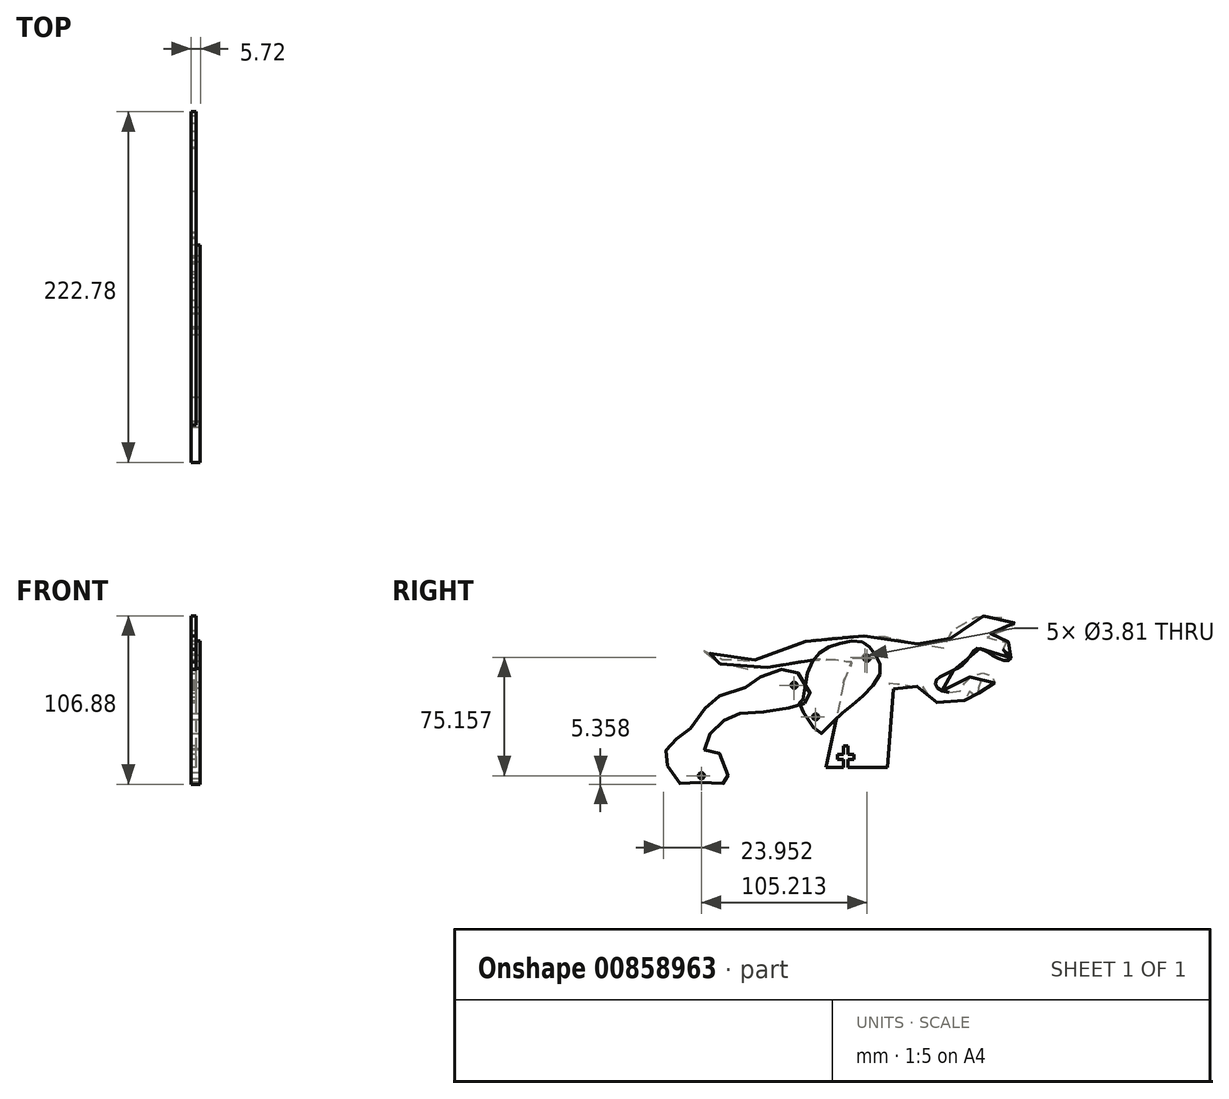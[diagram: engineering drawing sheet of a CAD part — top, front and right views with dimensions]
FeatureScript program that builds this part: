
annotation { "Feature Type Name" : "Feature", "Feature Type Description" : "" }
export const myFeature = defineFeature(function(context is Context, id is Id, definition is map)
    precondition{}
    {
        {
            var Q0;
            Q0=qCreatedBy(makeId("Right.planeOp"),FACE);
            var sketch = newSketch(context, id + "F0", { "sketchPlane" : qUnion([Q0])});
            skLineSegment(sketch, "E0.bottom", {"start": v(-101.6, -58.23) * mm, "end": v(101.6, -58.23) * mm});
            skLineSegment(sketch, "E0.top", {"start": v(-101.6, 43.37) * mm, "end": v(101.6, 43.37) * mm});
            skLineSegment(sketch, "E0.left", {"start": v(-101.6, -58.23) * mm, "end": v(-101.6, 43.37) * mm});
            skLineSegment(sketch, "E0.right", {"start": v(101.6, -58.23) * mm, "end": v(101.6, 43.37) * mm});
            skFitSpline(sketch, "E1", {"points": [v(-99.09, 21.53) * mm, v(-88.71, 16.38) * mm, v(-70.91, 13.77) * mm, v(-51.8, 19.14) * mm, v(-25.55, 28.4) * mm, v(4.08, 29.94) * mm, v(29.4, 27.78) * mm, v(49.76, 21.92) * mm, v(57.79, 25) * mm, v(61.18, 35.19) * mm, v(76.93, 42.29) * mm, v(90.82, 41.98) * mm, v(98.84, 39.51) * mm, v(99.63, 37.46) * mm, v(98.96, 34.1) * mm, v(95.6, 33.6) * mm, v(81.8, 30.57) * mm, v(82.64, 28.88) * mm, v(90.38, 25.01) * mm, v(97.27, 26.7) * mm, v(92.4, 21.82) * mm, v(96.94, 17.28) * mm, v(96.1, 14.42) * mm, v(86, 17.44) * mm, v(75.74, 22.15) * mm, v(70.19, 15.26) * mm, v(58.41, 7.01) * mm, v(49.67, 1.46) * mm, v(51.85, -3.92) * mm, v(64.97, -5.1) * mm, v(68.84, 1.63) * mm, v(79.27, 6.34) * mm, v(86.5, 3.31) * mm, v(86.84, 0) * mm, v(83.14, 1.63) * mm, v(76.92, 0) * mm, v(76.92, -6.78) * mm, v(73.9, -8.46) * mm, v(72.04, -4.43) * mm, v(67.33, -11.66) * mm, v(64.97, -11.66) * mm, v(54.71, -11.32) * mm, v(49.16, -12) * mm, v(42.1, -2.74) * mm, v(41.6, -1.4) * mm, v(33.68, -2.24) * mm, v(20.06, 0) * mm, v(22.74, -3.75) * mm, v(0, -3.58) * mm, v(-8.88, 0) * mm, v(-3.5, 12.9) * mm, v(-5.68, 13.4) * mm, v(-10.9, 14.25) * mm, v(-31.08, 14.75) * mm, v(-49.08, 11.9) * mm, v(-66.3, 8.68) * mm, v(-86.1, 11.83) * mm, v(-99.09, 20.33) * mm, v(-99.09, 21.53) * mm]});
            skLineSegment(sketch, "E2", {"start": v(-8.88, 0) * mm, "end": v(-8.88, -0.42) * mm});
            skLineSegment(sketch, "E3", {"start": v(-6.19, -53.65) * mm, "end": v(19.06, -53.65) * mm});
            skLineSegment(sketch, "E4", {"start": v(19.06, -53.65) * mm, "end": v(22.74, -3.75) * mm});
            skPoint(sketch, "E5", {"position": v(5.1, -53.65) * mm});
            skPoint(sketch, "E6", {"position": v(11.44, -53.65) * mm});
            skPoint(sketch, "E7", {"position": v(-1.26, -53.65) * mm});
            skLineSegment(sketch, "E8.bottom", {"start": v(-1.26, -53.65) * mm, "end": v(11.44, -53.65) * mm});
            skLineSegment(sketch, "E8.top", {"start": v(-1.26, -57.46) * mm, "end": v(11.44, -57.46) * mm});
            skLineSegment(sketch, "E8.left", {"start": v(-1.26, -53.65) * mm, "end": v(-1.26, -57.46) * mm});
            skLineSegment(sketch, "E8.right", {"start": v(11.44, -53.65) * mm, "end": v(11.44, -57.46) * mm});
            skFitSpline(sketch, "E9", {"points": [v(-38.83, -1.02) * mm, v(-43.34, -9.03) * mm, v(-45.18, -18.35) * mm, v(-45.97, -18.87) * mm, v(-38.83, -29.37) * mm, v(-37.3, -28.72) * mm, v(-32.31, -23.6) * mm, v(-23.65, -16.25) * mm, v(-17.22, -7.19) * mm, v(-19.58, -1.02) * mm, v(-23.39, 2.79) * mm, v(-31.26, 2.4) * mm, v(-38.83, -1.02) * mm]});
            skFitSpline(sketch, "E10", {"points": [v(-69.17, -12.02) * mm, v(-65.16, -9.2) * mm, v(-59.21, -6.38) * mm, v(-52.14, -5.65) * mm, v(-49.52, -9.26) * mm, v(-45.79, -16) * mm, v(-48.07, -17.65) * mm, v(-51.2, -18.53) * mm, v(-57.32, -20.03) * mm, v(-68.85, -21.17) * mm, v(-73.17, -21.7) * mm, v(-77.93, -24.73) * mm, v(-82.13, -29.08) * mm, v(-83.8, -34) * mm, v(-82.63, -33.83) * mm, v(-78.1, -35.68) * mm, v(-75.34, -43.63) * mm, v(-75.27, -45.77) * mm, v(-78.96, -45.77) * mm, v(-87.61, -45.77) * mm, v(-92.9, -45.77) * mm, v(-97.04, -39.01) * mm, v(-97.84, -34.82) * mm, v(-95.26, -33.16) * mm, v(-92.9, -29.4) * mm, v(-89.03, -26.91) * mm, v(-83.5, -19.37) * mm, v(-79.67, -15.56) * mm, v(-69.17, -12.02) * mm]});
            skCircle(sketch, "E11", {"center": v(-84.74, -43.25) * mm, "radius": 1.06 * mm});
            skCircle(sketch, "E12", {"center": v(-52.03, -11.32) * mm, "radius": 1.06 * mm});
            skCircle(sketch, "E13", {"center": v(-40.2, -23.6) * mm, "radius": 1.06 * mm});
            skCircle(sketch, "E14", {"center": v(-22.06, -2.93) * mm, "radius": 1.06 * mm});
            skLineSegment(sketch, "E15", {"start": v(-20.2, -53.65) * mm, "end": v(-9.03, -53.65) * mm});
            skLineSegment(sketch, "E16", {"start": v(-8.88, -0.42) * mm, "end": v(-20.2, -53.65) * mm});
            skPoint(sketch, "E17", {"position": v(-6.19, -53.65) * mm});
            skLineSegment(sketch, "E18", {"start": v(-6.19, -53.65) * mm, "end": v(-6.19, -48.57) * mm});
            skLineSegment(sketch, "E19", {"start": v(-6.19, -48.57) * mm, "end": v(-2.28, -48.57) * mm});
            skLineSegment(sketch, "E20", {"start": v(-2.28, -48.57) * mm, "end": v(-2.28, -45.4) * mm});
            skLineSegment(sketch, "E21", {"start": v(-2.28, -45.4) * mm, "end": v(-6.19, -45.4) * mm});
            skLineSegment(sketch, "E22", {"start": v(-6.19, -45.4) * mm, "end": v(-6.19, -39.8) * mm});
            skLineSegment(sketch, "E23", {"start": v(-6.19, -39.8) * mm, "end": v(-7.6, -39.8) * mm});
            skPoint(sketch, "E24.orphan", {"position": v(-8.88, -53.65) * mm});
            skLineSegment(sketch, "E25.MirrorCS", {"start": v(-9.03, -39.8) * mm, "end": v(-7.6, -39.8) * mm});
            skLineSegment(sketch, "E26.MirrorCS", {"start": v(-9.03, -45.4) * mm, "end": v(-9.03, -39.8) * mm});
            skLineSegment(sketch, "E27.MirrorCS", {"start": v(-12.93, -45.4) * mm, "end": v(-9.03, -45.4) * mm});
            skLineSegment(sketch, "E28.MirrorCS", {"start": v(-12.93, -48.57) * mm, "end": v(-12.93, -45.4) * mm});
            skLineSegment(sketch, "E29.MirrorCS", {"start": v(-9.03, -48.57) * mm, "end": v(-12.93, -48.57) * mm});
            skLineSegment(sketch, "E30.MirrorCS", {"start": v(-9.03, -53.65) * mm, "end": v(-9.03, -48.57) * mm});
            skCircle(sketch, "E31", {"center": v(4.79, 16.35) * mm, "radius": 1.9 * mm});
            skSolve(sketch);
        }
        {
            var Q0;
            Q0=makeQuery(id+"F0.imprint","IMPRINT",FACE,{"disambiguationData":[TD([[makeQuery(id+"F0.imprint","IMPRINT",EDGE,{"derivedFrom":sQuery(id+"F0.wireOp",EDGE,"E1")}),-1.0]])]});
            var Q1;
            {var subQ5=sQuery(id+"F0.wireOp",EDGE,"E3");Q1=makeQuery(id+"F0.imprint","IMPRINT",FACE,{"disambiguationData":[TD([[makeQuery(id+"F0.imprint","IMPRINT",EDGE,{"derivedFrom":subQ5}),1.0]])]});}
            var Q2;
            Q2=makeQuery(id+"F0.imprint","IMPRINT",FACE,{"disambiguationData":[TD([[makeQuery(id+"F0.imprint","IMPRINT",EDGE,{"derivedFrom":sQuery(id+"F0.wireOp",EDGE,"E8.bottom")}),-1.0]])]});
            extrude(context, id + "F1", {"entities" : qUnion([Q0, Q1, Q2]), "depth" : 3.17 * mm, "offsetDistance" : 25.4 * mm});
        }
        {
            var Q0;
            Q0=makeQuery(id+"F0.imprint","IMPRINT",FACE,{"disambiguationData":[TD([[makeQuery(id+"F0.imprint","IMPRINT",EDGE,{"derivedFrom":sQuery(id+"F0.wireOp",EDGE,"E9")}),1.0]])]});
            extrude(context, id + "F2", {"entities" : qUnion([Q0]), "depth" : 3.17 * mm, "offsetDistance" : 25.4 * mm});
        }
        {
            var Q0;
            Q0=makeQuery(id+"F0.imprint","IMPRINT",FACE,{"disambiguationData":[TD([[makeQuery(id+"F0.imprint","IMPRINT",EDGE,{"derivedFrom":sQuery(id+"F0.wireOp",EDGE,"E10")}),-1.0]])]});
            extrude(context, id + "F3", {"entities" : qUnion([Q0]), "depth" : 3.17 * mm, "offsetDistance" : 25.4 * mm});
        }
        {
            var Q0;
            Q0=makeQuery(id+"F2.opExtrude","SWEPT_BODY",BODY,{"disambiguationData":[OSD([sQuery(id+"F0.wireOp",EDGE,"E9")])]});
            var Q1;
            Q1=qCreatedBy(makeId("Origin.pointOp"),VERTEX);
            var Q2;
            Q2=qCreatedBy(makeId("Origin.pointOp"),VERTEX);
            transform(context, id + "F4", {"entities" : qUnion([Q0]), "transformType" : TransformType.SCALE_UNIFORMLY, "scale" : 1.8, "scalePoint" : qUnion([Q2]), "makeCopy" : false});
        }
        {
            var Q0;
            Q0=makeQuery(id+"F2.opExtrude","SWEPT_BODY",BODY,{"disambiguationData":[OSD([sQuery(id+"F0.wireOp",EDGE,"E9")])]});
            transform(context, id + "F5", {"entities" : qUnion([Q0]), "transformType" : TransformType.TRANSLATION_3D, "dx" : 0 * mm, "dy" : 45.72 * mm, "dz" : 21.08 * mm, "makeCopy" : false});
        }
        {
            var Q0;
            Q0=makeQuery(id+"F3.opExtrude","SWEPT_BODY",BODY,{"disambiguationData":[OSD([sQuery(id+"F0.wireOp",EDGE,"E10")])]});
            var Q1;
            Q1=qCreatedBy(makeId("Origin.pointOp"),VERTEX);
            transform(context, id + "F6", {"entities" : qUnion([Q0]), "transformType" : TransformType.SCALE_UNIFORMLY, "scale" : 1.8, "scalePoint" : qUnion([Q1]), "makeCopy" : false});
        }
        {
            var Q0;
            Q0=makeQuery(id+"F3.opExtrude","SWEPT_BODY",BODY,{"disambiguationData":[OSD([sQuery(id+"F0.wireOp",EDGE,"E10")])]});
            transform(context, id + "F7", {"entities" : qUnion([Q0]), "transformType" : TransformType.TRANSLATION_3D, "dx" : 0 * mm, "dy" : 53.34 * mm, "dz" : 19.05 * mm, "makeCopy" : false});
        }
    });
